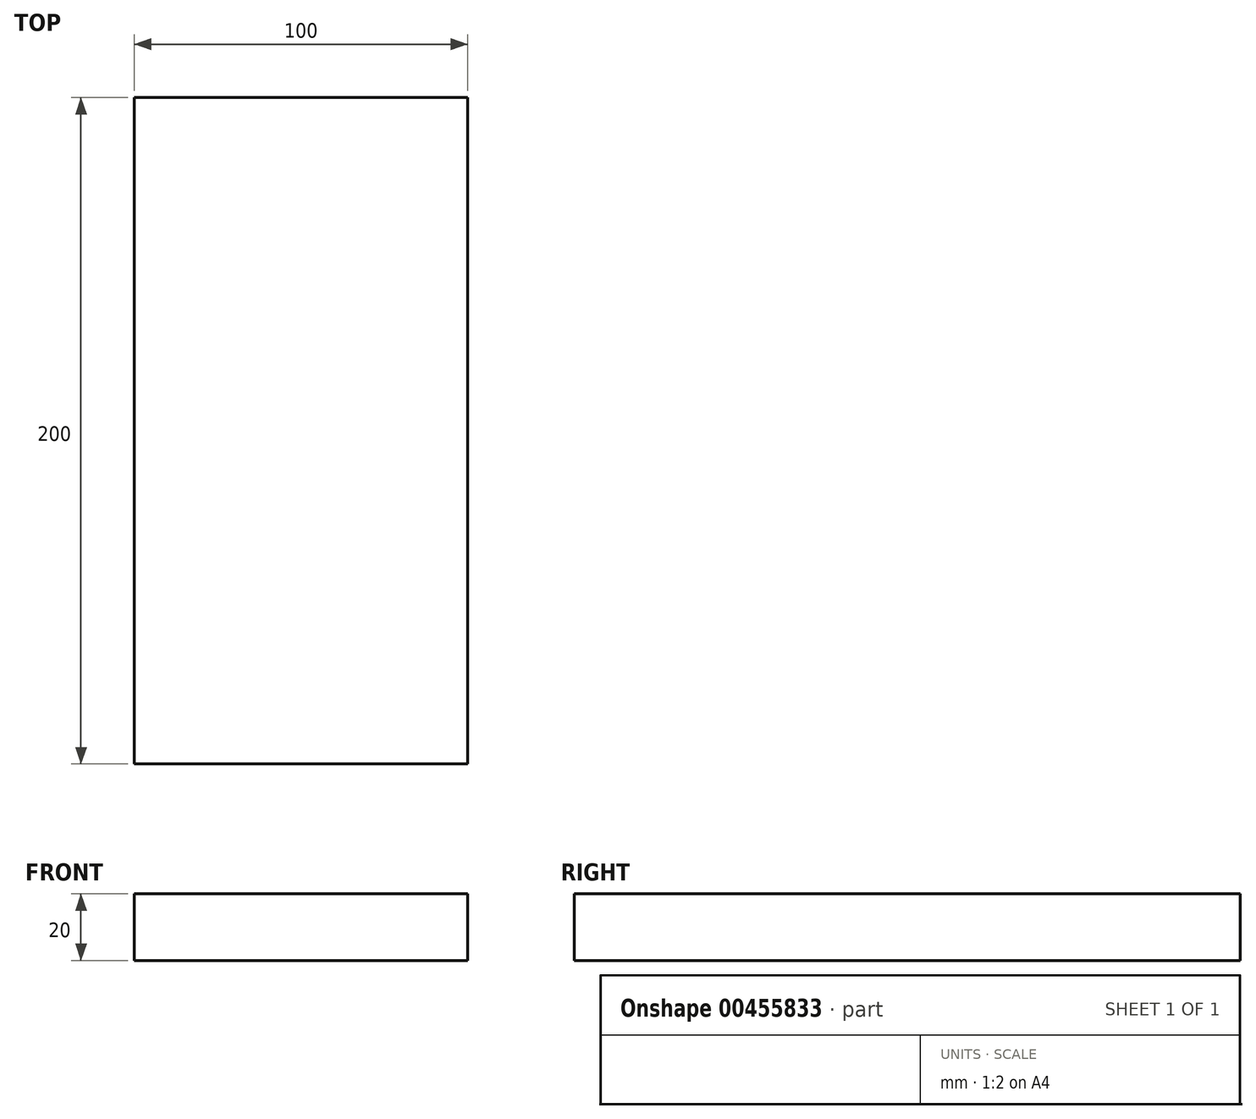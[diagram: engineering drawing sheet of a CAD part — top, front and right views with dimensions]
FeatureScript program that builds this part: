
annotation { "Feature Type Name" : "Feature", "Feature Type Description" : "" }
export const myFeature = defineFeature(function(context is Context, id is Id, definition is map)
    precondition{}
    {
        {
            assignVariable(context, id + "F0", {"name" : "Y", "anyValue" : 200});
        }
        {
            var Q0;
            Q0=qCreatedBy(makeId("Front.planeOp"),FACE);
            var sketch = newSketch(context, id + "F1", { "sketchPlane" : qUnion([Q0])});
            skLineSegment(sketch, "E0", {"start": v(0, 0) * mm, "end": v(100, 0) * mm});
            skLineSegment(sketch, "E1", {"start": v(100, 0) * mm, "end": v(100, 20) * mm});
            skLineSegment(sketch, "E2", {"start": v(100, 20) * mm, "end": v(0, 20) * mm});
            skLineSegment(sketch, "E3", {"start": v(0, 20) * mm, "end": v(0, 0) * mm});
            skSolve(sketch);
        }
        {
            var Q0;
            Q0=makeQuery(id+"F1.imprint","IMPRINT",FACE,{"disambiguationData":[TD([[makeQuery(id+"F1.imprint","IMPRINT",EDGE,{"derivedFrom":sQuery(id+"F1.wireOp",EDGE,"E0")}),1.0]])]});
            extrude(context, id + "F2", {"entities" : qUnion([Q0]), "depth" : getVariable(context, 'Y') * mm});
        }
    });
